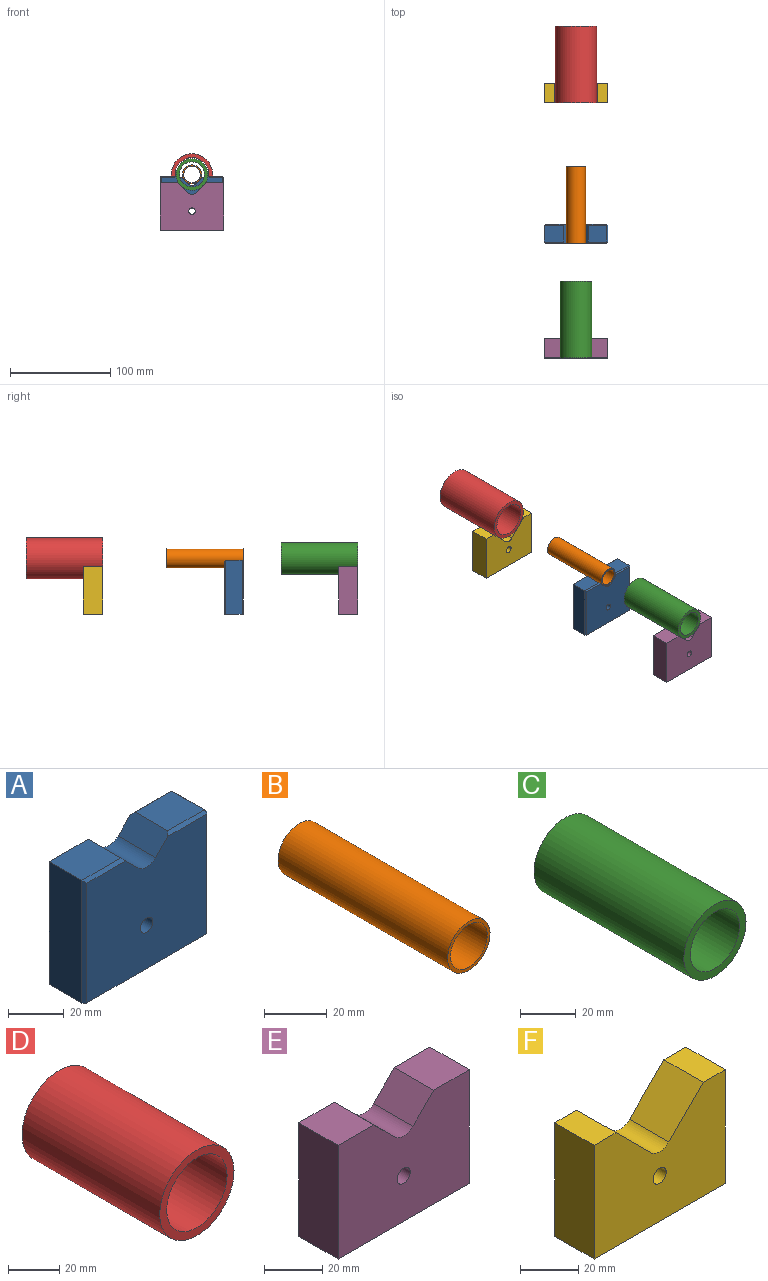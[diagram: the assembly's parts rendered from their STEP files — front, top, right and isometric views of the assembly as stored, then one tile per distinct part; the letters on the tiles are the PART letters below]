
ASSEMBLY  parts=6 mates=7
PART A: 28 faces, bbox 63.5x19.1x54 mm
  f0: cylinder r=3.17mm len=19.05mm, axis (0,-1,0), area 357.3mm2, adj f2,f3,f15
  f1: plane 18.51x16.51mm, normal (0,0,1), area 305.6mm2, adj f8,f20,f22,f23
  f2: plane 60.96x52.71mm, normal (0,-1,0), area 3075.4mm2, adj f0,f5,f8,f9,f10,f19,f20,f26
  f3: plane 60.96x52.71mm, normal (0,1,0), area 3075.4mm2, adj f0,f5,f8,f9,f10,f17,f18,f23
  f4: plane 53.98x16.51mm, normal (-1,0,0), area 891.1mm2, adj f5,f7,f18,f26
  f5: plane 63.5x19.05mm, normal (0,0,-1), area 1093.6mm2, adj f2,f3,f4,f6,f12,f14,f16,f18
  f6: plane 52.71x16.51mm, normal (1,0,0), area 870.2mm2, adj f5,f19,f22,f25
  f7: plane 19.78x16.51mm, normal (0,0,1), area 326.5mm2, adj f4,f9,f17,f27
  f8: plane 19.05x7.48mm, normal (-0.71,0,0.71), area 199.3mm2, adj f1,f2,f3,f10,f20,f23
  f9: plane 19.05x7.48mm, normal (0.71,0,0.71), area 199.3mm2, adj f2,f3,f7,f10,f17,f27
  f10: cylinder r=6.35mm len=19.05mm, axis (0,-1,0), area 190mm2, adj f2,f3,f8,f9
  f11: cone r=0mm half-angle=59deg, axis (0,0,-1), area 39mm2, adj f12
  f12: cylinder r=3.26mm len=19.05mm, axis (0,0,-1), area 390.7mm2, adj f5,f11
  f13: cone r=0mm half-angle=59deg, axis (0,0,-1), area 39mm2, adj f14
  f14: cylinder r=3.26mm len=19.05mm, axis (0,0,-1), area 390.7mm2, adj f5,f13
  f15: cylinder r=2.55mm len=15.89mm, axis (0,0,-1), area 243.9mm2, adj f0,f16
  f16: cone r=2.55mm half-angle=45deg, axis (0,0,-1), area 36mm2, adj f5,f15
  f17: plane 21.05x1.27mm, normal (0,0.71,0.71), area 35.5mm2, adj f3,f7,f9,f18
  f18: plane 53.98x1.27mm, normal (-0.71,0.71,0), area 95.8mm2, adj f3,f4,f5,f17
  f19: plane 52.71x1.27mm, normal (0.71,-0.71,0), area 94.7mm2, adj f2,f5,f6,f21
  f20: plane 19.78x1.27mm, normal (0,-0.71,0.71), area 34.4mm2, adj f1,f2,f8,f21
  f21: plane 1.27x1.27mm, normal (0.58,-0.58,0.58), area 1.4mm2, adj f19,f20,f22
  f22: plane 16.51x1.27mm, normal (0.71,0,0.71), area 29.7mm2, adj f1,f6,f21,f24
  f23: plane 19.78x1.27mm, normal (0,0.71,0.71), area 34.4mm2, adj f1,f3,f8,f24
  f24: plane 1.27x1.27mm, normal (0.58,0.58,0.58), area 1.4mm2, adj f22,f23,f25
  f25: plane 52.71x1.27mm, normal (0.71,0.71,0), area 94.7mm2, adj f3,f5,f6,f24
  f26: plane 53.98x1.27mm, normal (-0.71,-0.71,0), area 95.8mm2, adj f2,f4,f5,f27
  f27: plane 21.05x1.27mm, normal (0,-0.71,0.71), area 35.5mm2, adj f2,f7,f9,f26
PART B: 4 faces, bbox 19.1x76.2x19.1 mm
  f0: cylinder r=8.28mm len=76.2mm, axis (0,1,0), area 3964.5mm2, adj f2,f3
  f1: cylinder r=9.53mm len=76.2mm, axis (0,1,0), area 4560.4mm2, adj f2,f3
  f2: plane 19.05x19.05mm, normal (0,-1,0), area 69.6mm2, adj f0,f1
  f3: plane 19.05x19.05mm, normal (0,1,0), area 69.6mm2, adj f0,f1
PART C: 4 faces, bbox 31.6x76.2x31.6 mm
  f0: cylinder r=12.46mm len=76.2mm, axis (0,1,0), area 5965mm2, adj f2,f3
  f1: cylinder r=15.81mm len=76.2mm, axis (0,1,0), area 7570.2mm2, adj f2,f3
  f2: plane 31.62x31.62mm, normal (0,-1,0), area 297.8mm2, adj f0,f1
  f3: plane 31.62x31.62mm, normal (0,1,0), area 297.8mm2, adj f0,f1
PART D: 4 faces, bbox 41x76.2x41 mm
  f0: cylinder r=16.69mm len=76.2mm, axis (0,1,0), area 7989.8mm2, adj f2,f3
  f1: cylinder r=20.52mm len=76.2mm, axis (0,1,0), area 9826.1mm2, adj f2,f3
  f2: plane 41.05x41.05mm, normal (0,-1,0), area 448.4mm2, adj f0,f1
  f3: plane 41.05x41.05mm, normal (0,1,0), area 448.4mm2, adj f0,f1
PART E: 11 faces, bbox 63.5x19.1x47.6 mm
  f0: plane 19.05x17.22mm, normal (0,0,1), area 328mm2, adj f1,f2,f5,f8
  f1: plane 63.5x47.63mm, normal (0,-1,0), area 2790.1mm2, adj f0,f3,f4,f5,f6,f7,f8,f9
  f2: plane 63.5x47.63mm, normal (0,1,0), area 2790.1mm2, adj f0,f3,f4,f5,f6,f7,f8,f9
  f3: plane 47.63x19.05mm, normal (-1,0,0), area 907.3mm2, adj f1,f2,f4,f6
  f4: plane 63.5x19.05mm, normal (0,0,-1), area 1209.7mm2, adj f1,f2,f3,f5
  f5: plane 47.63x19.05mm, normal (1,0,0), area 907.3mm2, adj f0,f1,f2,f4
  f6: plane 19.05x17.22mm, normal (0,0,1), area 328mm2, adj f1,f2,f3,f9
  f7: cylinder r=3.17mm len=19.05mm, axis (0,-1,0), area 380mm2, adj f1,f2
  f8: plane 19.05x10.04mm, normal (-0.71,0,0.71), area 270.5mm2, adj f0,f1,f2,f10
  f9: plane 19.05x10.04mm, normal (0.71,0,0.71), area 270.5mm2, adj f1,f2,f6,f10
  f10: cylinder r=6.35mm len=19.05mm, axis (0,-1,0), area 190mm2, adj f1,f2,f8,f9
PART F: 11 faces, bbox 63.5x19.1x47.6 mm
  f0: plane 19.05x10.65mm, normal (0,0,1), area 202.8mm2, adj f1,f2,f5,f8
  f1: plane 63.5x47.63mm, normal (0,-1,0), area 2555.8mm2, adj f0,f3,f4,f5,f6,f7,f8,f9
  f2: plane 63.5x47.63mm, normal (0,1,0), area 2555.8mm2, adj f0,f3,f4,f5,f6,f7,f8,f9
  f3: plane 47.63x19.05mm, normal (-1,0,0), area 907.3mm2, adj f1,f2,f4,f6
  f4: plane 63.5x19.05mm, normal (0,0,-1), area 1209.7mm2, adj f1,f2,f3,f5
  f5: plane 47.63x19.05mm, normal (1,0,0), area 907.3mm2, adj f0,f1,f2,f4
  f6: plane 19.05x10.65mm, normal (0,0,1), area 202.8mm2, adj f1,f2,f3,f9
  f7: cylinder r=3.17mm len=19.05mm, axis (0,-1,0), area 380mm2, adj f1,f2
  f8: plane 19.05x16.61mm, normal (-0.71,0,0.71), area 447.6mm2, adj f0,f1,f2,f10
  f9: plane 19.05x16.61mm, normal (0.71,0,0.71), area 447.6mm2, adj f1,f2,f6,f10
  f10: cylinder r=6.35mm len=19.05mm, axis (0,-1,0), area 190mm2, adj f1,f2,f8,f9
PLACE A t=(-50.29,-125.16,-45.78)mm
PLACE B t=(-18.54,-68.01,9.84)mm
PLACE C rot(axis=(0,1,0),26.8deg) t=(-18.54,-182.12,9.87)mm
PLACE D t=(-18.54,72.23,9.95)mm
PLACE E t=(-50.29,-239.27,-45.78)mm
PLACE F t=(-50.29,15.08,-45.78)mm fixed
MATE cylindrical E.f7 <-> F.f7  axis (0,-1,0) through (-18.54,-258.32,-26.73)mm
MATE planar F.f4 <-> E.f4  axis (0,0,-1) through (-18.54,5.55,-45.78)mm
MATE planar C.f1 <-> E.f1  axis (0,-1,0) through (-18.54,-258.32,9.87)mm
MATE planar B.f1 <-> A.f2  axis (0,-1,0) through (-18.54,-144.21,9.84)mm
MATE cylindrical A.f0 <-> F.f7  axis (0,-1,0) through (-18.54,-144.21,-26.73)mm
MATE cylindrical F.f7 <-> E.f7  axis (0,-1,0) through (-18.54,5.55,-26.73)mm
MATE planar D.f1 <-> F.f1  axis (0,-1,0) through (-18.54,-3.97,9.95)mm
